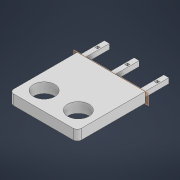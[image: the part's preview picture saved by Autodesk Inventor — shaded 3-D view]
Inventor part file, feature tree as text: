
AUTODESK INVENTOR PART (.ipt)
format: ipt  version: 2022 (Build 260153000, 153)  size: 312,832 bytes
history: native  units: in
note: dims shown in document units (in); Inventor stores cm internally (conversion verified against a paired STEP export)
features: reference x16, extrude x4, sketch x4, other x4, plane x2, fillet x1
ambient origin geometry x8: Origin, YZ Plane, XZ Plane, XY Plane, X Axis, Y Axis, Z Axis, Center Point
bodies: Solid1 (feature_tree)
feature tree (31):
  plane  "Work Plane1"
  extrude  "Extrusion1"  Depth=0.15in TaperAngle=0.0deg
  extrude  "Extrusion2"  Depth=2.0in
  plane  "Work Plane2"
  extrude  "Extrusion3"  Depth=0.5363in
  extrude  "Extrusion4"  Depth=0.125in
  fillet  "Fillet1"  Radius=0.0344in
  sketch  "Sketch1"  dims[d0=0.75in d1=0.0in d2=0.15in d3=0.0in]
  reference  "Reference1"
  sketch  "Sketch2"  dims[d4=2.0in d5=0.0in d6=0.626in]
  reference  "Reference2"
  reference  "Reference3"
  reference  "Reference4"
  reference  "Reference5"
  reference  "Reference6"
  reference  "Reference7"
  reference  "Reference8"
  reference  "Reference9"
  reference  "Reference10"
  reference  "Reference11"
  reference  "Reference12"
  reference  "Reference13"
  sketch  "Sketch3"  dims[d7=0.626in d8=0.5363in]
  reference  "Reference14"
  sketch  "Sketch4"  dims[d9=0.3in d10=0.0in d11=0.125in d12=0.0344in]
  reference  "Reference15"
  reference  "Reference16"
  parser-record x1  (decoder bookkeeping rows leaked as tree rows — omitted from the tree; the rows remain in map.json)
  other  "Prototype Assembly.iam"
  other  "Vertical Beam Prototype:1"
  other  "hc-sr04:1"
note: 1 file-system path scrubbed to <path> (originals preserved in map.json)
